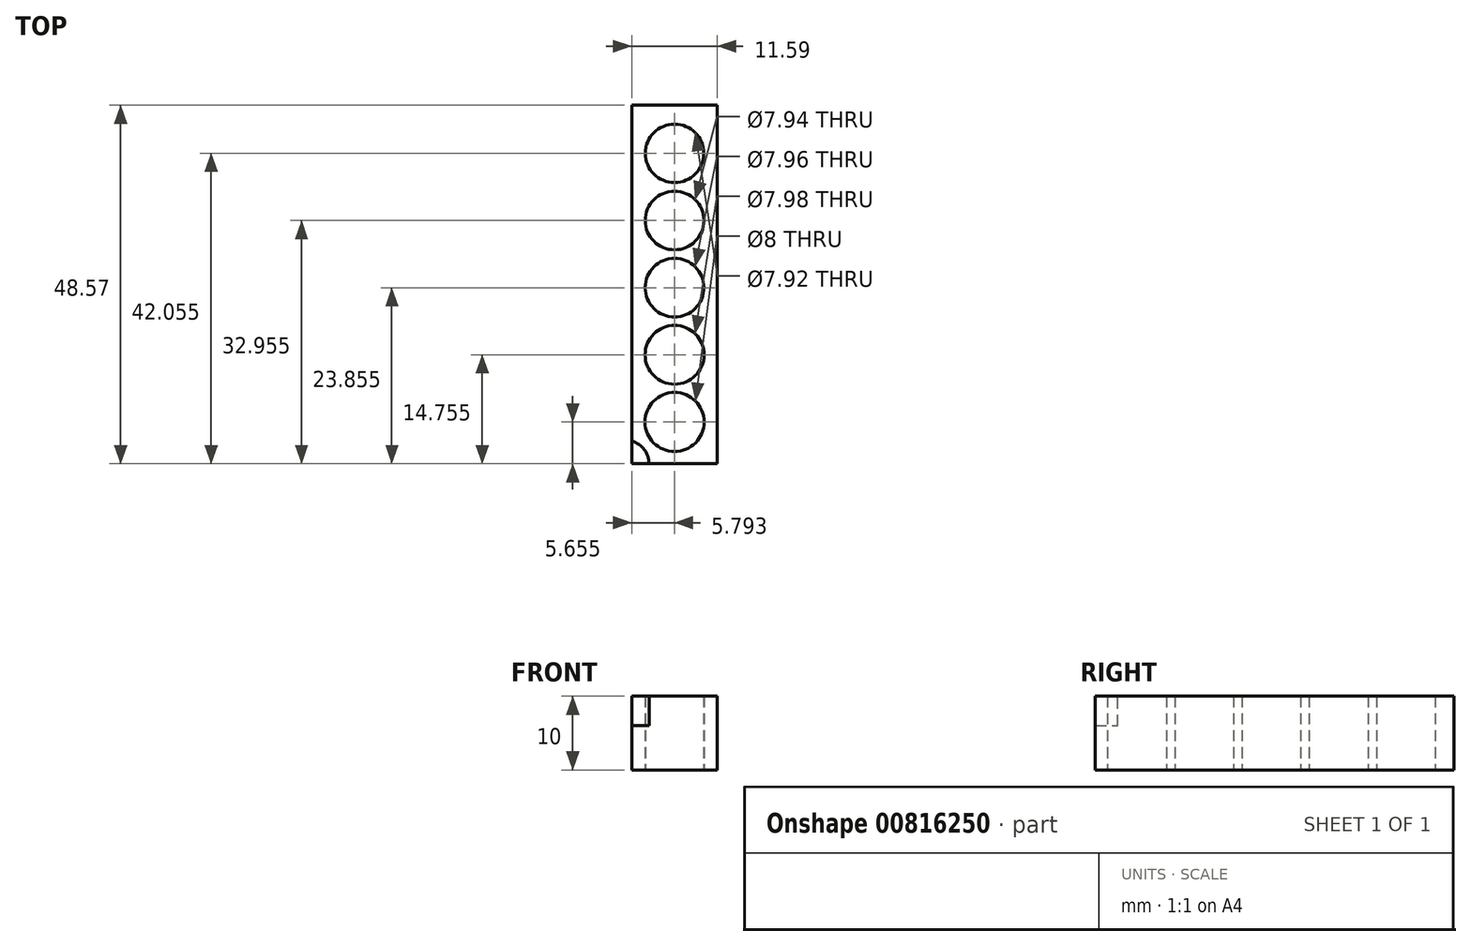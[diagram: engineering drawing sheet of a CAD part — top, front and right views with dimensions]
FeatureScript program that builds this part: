
annotation { "Feature Type Name" : "Feature", "Feature Type Description" : "" }
export const myFeature = defineFeature(function(context is Context, id is Id, definition is map)
    precondition{}
    {
        {
            var Q0;
            Q0=qCreatedBy(makeId("Top.planeOp"),FACE);
            var sketch = newSketch(context, id + "F0", { "sketchPlane" : qUnion([Q0])});
            skLineSegment(sketch, "E0.bottom", {"start": v(0, 0) * mm, "end": v(11.59, 0) * mm});
            skLineSegment(sketch, "E0.top", {"start": v(0, 48.57) * mm, "end": v(11.59, 48.57) * mm});
            skLineSegment(sketch, "E0.left", {"start": v(0, 0) * mm, "end": v(0, 48.57) * mm});
            skLineSegment(sketch, "E0.right", {"start": v(11.59, 0) * mm, "end": v(11.59, 48.57) * mm});
            skPoint(sketch, "E1.centerSnap0", {"position": v(5.8, 0) * mm});
            skCircle(sketch, "E2", {"center": v(5.8, 5.66) * mm, "radius": 4 * mm});
            skCircle(sketch, "E3.0.1.0", {"center": v(5.8, 14.76) * mm, "radius": 4 * mm});
            skCircle(sketch, "E3.0.2.0", {"center": v(5.8, 23.86) * mm, "radius": 3.98 * mm});
            skCircle(sketch, "E3.0.3.0", {"center": v(5.8, 32.96) * mm, "radius": 3.97 * mm});
            skCircle(sketch, "E3.0.4.0", {"center": v(5.8, 42.06) * mm, "radius": 3.96 * mm});
            skLineSegment(sketch, "E3.direction2", {"start": v(5.8, 5.66) * mm, "end": v(5.8, 14.76) * mm, "construction": true});
            skSolve(sketch);
        }
        {
            var Q0;
            Q0 = qSketchRegion(id + "F0", true);
            extrude(context, id + "F1", {"entities" : qUnion([Q0]), "depth" : 10 * mm, "offsetDistance" : 25 * mm});
        }
        {
            var Q0;
            Q0=makeQuery(id+"F1.opExtrude","CAP_FACE",FACE,{"disambiguationData":[OSD([sQuery(id+"F0.wireOp",EDGE,"E0.bottom"),sQuery(id+"F0.wireOp",EDGE,"E0.top"),sQuery(id+"F0.wireOp",EDGE,"E0.left"),sQuery(id+"F0.wireOp",EDGE,"E0.right"),sQuery(id+"F0.wireOp",EDGE,"E2"),sQuery(id+"F0.wireOp",EDGE,"E3.0.1.0"),sQuery(id+"F0.wireOp",EDGE,"E3.0.2.0"),sQuery(id+"F0.wireOp",EDGE,"E3.0.3.0"),sQuery(id+"F0.wireOp",EDGE,"E3.0.4.0")])],"isStart":false});
            var sketch = newSketch(context, id + "F2", { "sketchPlane" : qUnion([Q0])});
            skCircle(sketch, "E4", {"center": v(-0.84, 0) * mm, "radius": 3.17 * mm});
            skSolve(sketch);
        }
        {
            var Q0;
            Q0 = qSketchRegion(id + "F2", true);
            extrude(context, id + "F3", {"entities" : qUnion([Q0]), "operationType" : NewBodyOperationType.REMOVE, "oppositeDirection" : true, "depth" : 4 * mm, "offsetDistance" : 25 * mm});
        }
    });
